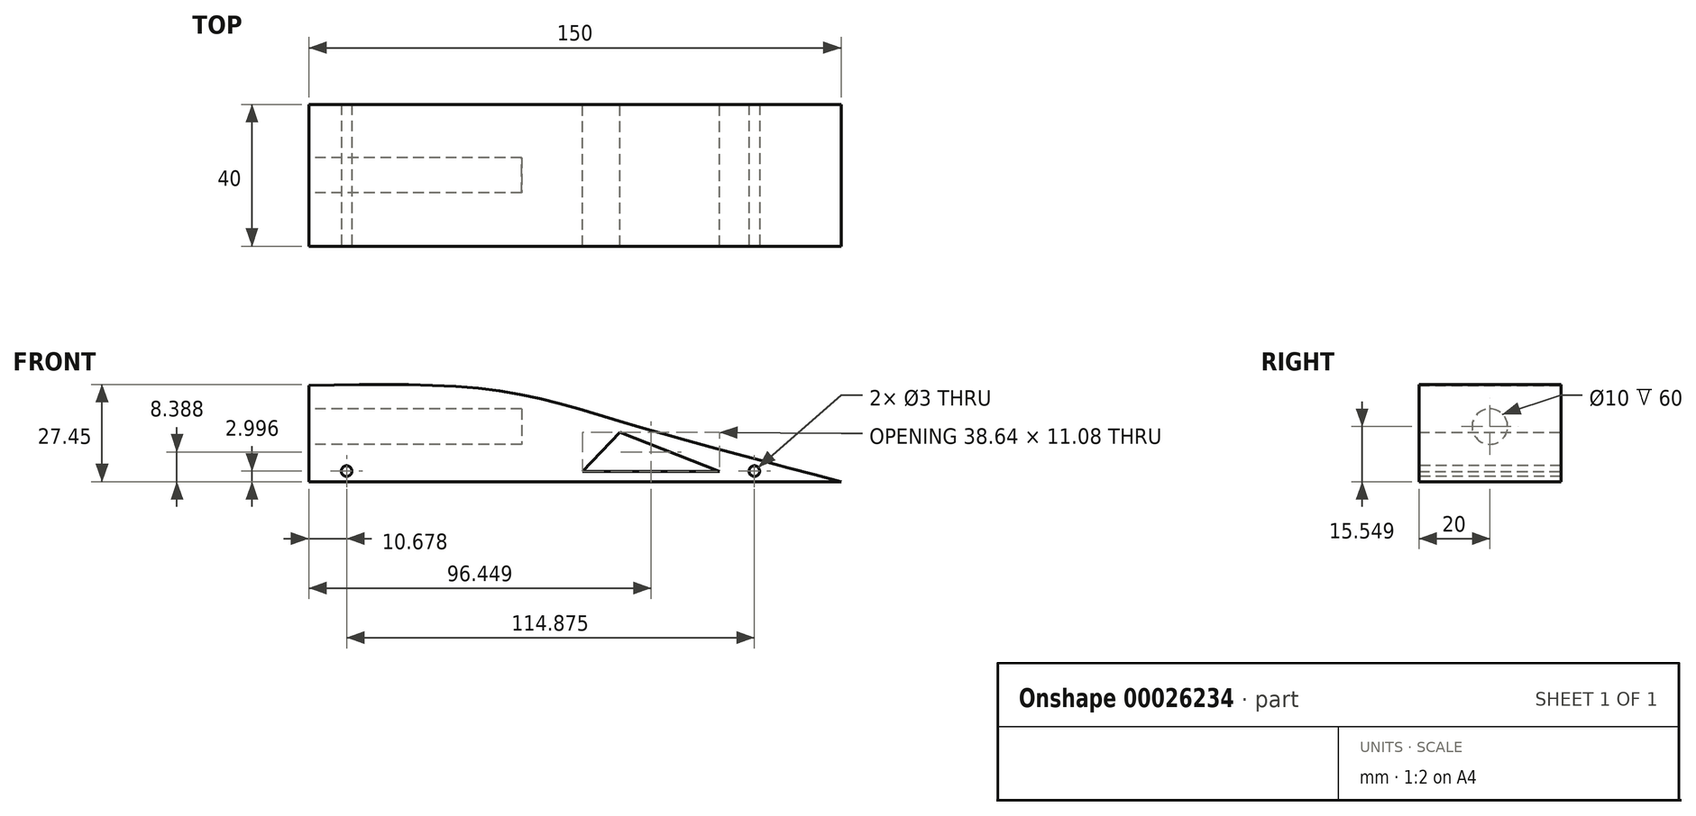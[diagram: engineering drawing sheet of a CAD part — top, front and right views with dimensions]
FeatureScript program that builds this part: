
annotation { "Feature Type Name" : "Feature", "Feature Type Description" : "" }
export const myFeature = defineFeature(function(context is Context, id is Id, definition is map)
    precondition{}
    {
        {
            var Q0;
            Q0=qCreatedBy(makeId("Front.planeOp"),FACE);
            var sketch = newSketch(context, id + "F0", { "sketchPlane" : qUnion([Q0])});
            skLineSegment(sketch, "E0.bottom", {"start": v(-42.07, -16.15) * mm, "end": v(107.93, -16.15) * mm});
            skLineSegment(sketch, "E0.left", {"start": v(-42.07, -16.15) * mm, "end": v(-42.07, 14.11) * mm});
            skLineSegment(sketch, "E1", {"start": v(-42.07, 14.11) * mm, "end": v(107.93, 14.11) * mm});
            skLineSegment(sketch, "E2", {"start": v(107.93, 14.11) * mm, "end": v(107.93, -16.15) * mm});
            skFitSpline(sketch, "E3", {"points": [v(-42.07, 11.02) * mm, v(10.63, 9.6) * mm, v(48.68, 0) * mm, v(107.93, -16.15) * mm], "startDerivative": vector(164.2, 3.21) * mm, "endDerivative": vector(172.53, -45.4) * mm});
            skLineSegment(sketch, "E4", {"start": v(45.6, -2.22) * mm, "end": v(35.06, -13.3) * mm});
            skLineSegment(sketch, "E5", {"start": v(35.06, -13.3) * mm, "end": v(73.7, -13.3) * mm});
            skLineSegment(sketch, "E6", {"start": v(73.7, -13.3) * mm, "end": v(45.6, -2.22) * mm});
            skSolve(sketch);
        }
        {
            var Q0;
            Q0=makeQuery(id+"F0.imprint","IMPRINT",FACE,{"disambiguationData":[TD([[makeQuery(id+"F0.imprint","IMPRINT",EDGE,{"derivedFrom":sQuery(id+"F0.wireOp",EDGE,"E0.bottom")}),1.0]])]});
            extrude(context, id + "F1", {"entities" : qUnion([Q0]), "depth" : 40 * mm});
        }
        {
            var Q0;
            Q0=makeQuery(id+"F1.opExtrude","SWEPT_FACE",FACE,{"disambiguationData":[OSD([sQuery(id+"F0.wireOp",EDGE,"E0.left")])]});
            var sketch = newSketch(context, id + "F2", { "sketchPlane" : qUnion([Q0])});
            skCircle(sketch, "E7", {"center": v(20, -0.6) * mm, "radius": 5 * mm});
            skSolve(sketch);
        }
        {
            var Q0;
            Q0=makeQuery(id+"F2.imprint","IMPRINT",FACE,{"disambiguationData":[TD([[makeQuery(id+"F2.imprint","IMPRINT",EDGE,{"derivedFrom":sQuery(id+"F2.wireOp",EDGE,"E7")}),1.0]])]});
            extrude(context, id + "F3", {"entities" : qUnion([Q0]), "operationType" : NewBodyOperationType.REMOVE, "oppositeDirection" : true, "depth" : 60 * mm});
        }
        {
            var Q0;
            Q0=makeQuery(id+"F1.opExtrude","CAP_FACE",FACE,{"disambiguationData":[OSD([sQuery(id+"F0.wireOp",EDGE,"E0.bottom"),sQuery(id+"F0.wireOp",EDGE,"E0.top"),sQuery(id+"F0.wireOp",EDGE,"E0.left"),sQuery(id+"F0.wireOp",EDGE,"E0.right")])],"isStart":false});
            var sketch = newSketch(context, id + "F4", { "sketchPlane" : qUnion([Q0])});
            skCircle(sketch, "E8", {"center": v(-31.4, -13.15) * mm, "radius": 1.5 * mm});
            skCircle(sketch, "E9", {"center": v(83.48, -13.15) * mm, "radius": 1.5 * mm});
            skSolve(sketch);
        }
        {
            var Q0;
            Q0=makeQuery(id+"F4.imprint","IMPRINT",FACE,{"disambiguationData":[TD([[makeQuery(id+"F4.imprint","IMPRINT",EDGE,{"derivedFrom":sQuery(id+"F4.wireOp",EDGE,"E8")}),1.0]])]});
            var Q1;
            Q1=makeQuery(id+"F4.imprint","IMPRINT",FACE,{"disambiguationData":[TD([[makeQuery(id+"F4.imprint","IMPRINT",EDGE,{"derivedFrom":sQuery(id+"F4.wireOp",EDGE,"E9")}),1.0]])]});
            extrude(context, id + "F5", {"entities" : qUnion([Q0, Q1]), "operationType" : NewBodyOperationType.REMOVE, "endBound" : BoundingType.THROUGH_ALL, "oppositeDirection" : true, "depth" : 25 * mm});
        }
    });
